# Revit family: NLRS_57_DUA_UN_rectangular smokesensor ug_sacs
name_source: partatom
category: Duct Accessories
units: mm (PartAtom-declared; Revit-internal decimal feet)

## family parameters
Always vertical = Yes
Cut with Voids When Loaded = No
Part Type = Breaks Into
Round Connector Dimension = Use Diameter
Shared = No
Work Plane-Based = No

## types (1)
- NLRS_57_DUA_UN_rectangular smokesensor ug_sacs
    Article_Data = UG_Article_Data
    Assembly Code = 57.70
    Casing material = Galvanized Steel
    Combo (do not change!) = No
    Description = Rechthoekige rook sensor voor FD25 of FD40
    FireRating = 0h
    IfcDescription = Rechthoekige rook sensor voor FD25 of FD40
    IfcExportAs = IfcDamperType
    IfcExportType = SMOKE SENSOR
    LoadBearing = No
    Manufacturer = Solid Air Climate Solutions
    Model = Koude rook sensor rechthoekig
    NLRS_C_content_datum_uitgifte = 14-01-2022
    NLRS_C_content_provider = Solid Air Climate Systems
    NLRS_C_content_versie = Versie 3.19.00
    NLRS_C_description = Rechthoekige rook sensor voor FD25 of FD40
    NLRS_C_niveau ontwikkeling = LOD400
    Type Comments = Check flow direction!
    URL = https://solid-air.nl

## geometry (parser evidence)
native form markers: Sweep x14
no freeform markers — native parametric forms only
